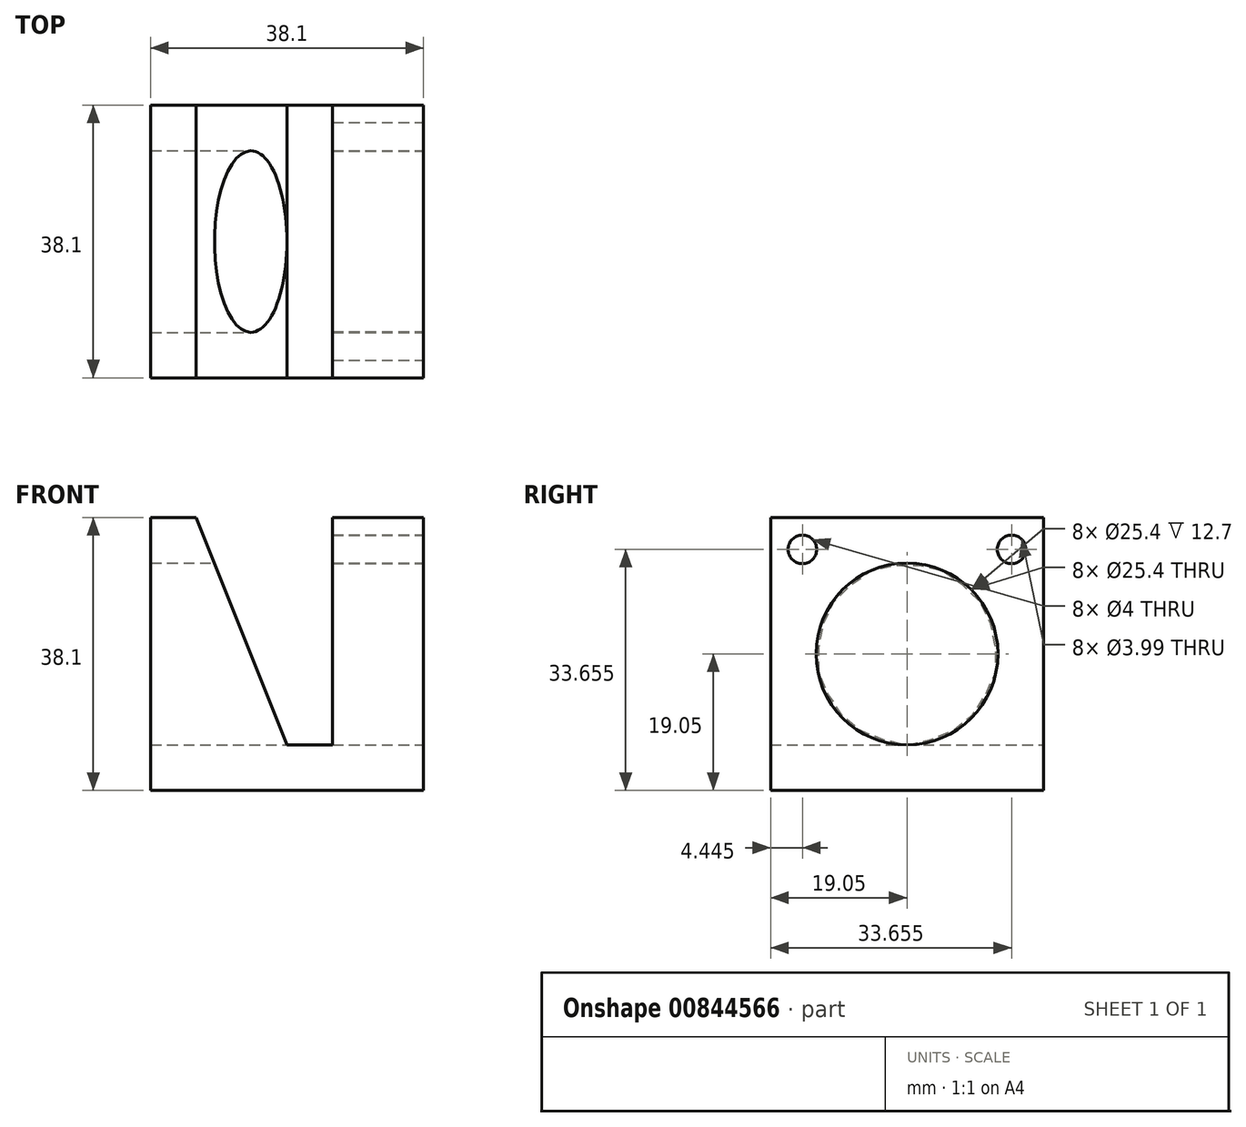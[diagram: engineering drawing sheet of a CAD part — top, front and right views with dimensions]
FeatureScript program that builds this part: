
annotation { "Feature Type Name" : "Feature", "Feature Type Description" : "" }
export const myFeature = defineFeature(function(context is Context, id is Id, definition is map)
    precondition{}
    {
        {
            var Q0;
            Q0=qCreatedBy(makeId("Front.planeOp"),FACE);
            var sketch = newSketch(context, id + "F0", { "sketchPlane" : qUnion([Q0])});
            skLineSegment(sketch, "E0.bottom", {"start": v(19.05, 19.05) * mm, "end": v(-19.05, 19.05) * mm});
            skLineSegment(sketch, "E0.top", {"start": v(19.05, -19.05) * mm, "end": v(-19.05, -19.05) * mm});
            skLineSegment(sketch, "E0.left", {"start": v(19.05, 19.05) * mm, "end": v(19.05, -19.05) * mm});
            skLineSegment(sketch, "E0.right", {"start": v(-19.05, 19.05) * mm, "end": v(-19.05, -19.05) * mm});
            skPoint(sketch, "E0.middle", {"position": v(0, 0) * mm});
            skLineSegment(sketch, "E1", {"start": v(6.35, 19.05) * mm, "end": v(6.35, -12.7) * mm});
            skLineSegment(sketch, "E2", {"start": v(6.35, -12.7) * mm, "end": v(0, -12.7) * mm});
            skLineSegment(sketch, "E3", {"start": v(-12.7, 19.05) * mm, "end": v(0, -12.7) * mm});
            skLineSegment(sketch, "E4", {"start": v(-12.7, 19.05) * mm, "end": v(-19.05, 19.05) * mm});
            skLineSegment(sketch, "E5", {"start": v(-12.7, 19.05) * mm, "end": v(-6.35, 19.05) * mm});
            skSolve(sketch);
        }
        {
            var Q0;
            Q0=makeQuery(id+"F0.imprint","IMPRINT",FACE,{"disambiguationData":[TD([[makeQuery(id+"F0.imprint","IMPRINT",EDGE,{"derivedFrom":sQuery(id+"F0.wireOp",EDGE,"E0.top")}),-1.0]])]});
            extrude(context, id + "F1", {"entities" : qUnion([Q0]), "endBound" : BoundingType.SYMMETRIC, "depth" : 38.1 * mm, "offsetDistance" : 25.4 * mm});
        }
        {
            var Q0;
            Q0=makeQuery(id+"F1.opExtrude","SWEPT_FACE",FACE,{"disambiguationData":[OSD([sQuery(id+"F0.wireOp",EDGE,"E0.left")])]});
            var sketch = newSketch(context, id + "F2", { "sketchPlane" : qUnion([Q0])});
            skCircle(sketch, "E6", {"center": v(0, 0) * mm, "radius": 12.7 * mm});
            skCircle(sketch, "E7", {"center": v(-14.6, 14.6) * mm, "radius": 2 * mm});
            skCircle(sketch, "E8", {"center": v(14.6, 14.6) * mm, "radius": 2 * mm});
            skSolve(sketch);
        }
        {
            var Q0;
            Q0=makeQuery(id+"F2.imprint","IMPRINT",FACE,{"disambiguationData":[TD([[makeQuery(id+"F2.imprint","IMPRINT",EDGE,{"derivedFrom":sQuery(id+"F2.wireOp",EDGE,"E6")}),1.0]])]});
            extrude(context, id + "F3", {"entities" : qUnion([Q0]), "operationType" : NewBodyOperationType.REMOVE, "oppositeDirection" : true, "depth" : 38.1 * mm, "offsetDistance" : 25.4 * mm});
        }
        {
            var Q0;
            Q0=makeQuery(id+"F2.imprint","IMPRINT",FACE,{"disambiguationData":[TD([[makeQuery(id+"F2.imprint","IMPRINT",EDGE,{"derivedFrom":sQuery(id+"F2.wireOp",EDGE,"E8")}),1.0]])]});
            var Q1;
            Q1=makeQuery(id+"F2.imprint","IMPRINT",FACE,{"disambiguationData":[TD([[makeQuery(id+"F2.imprint","IMPRINT",EDGE,{"derivedFrom":sQuery(id+"F2.wireOp",EDGE,"E7")}),1.0]])]});
            var Q2;
            Q2=makeQuery(id+"F2.imprint","IMPRINT",FACE,{"disambiguationData":[TD([[makeQuery(id+"F2.imprint","IMPRINT",EDGE,{"derivedFrom":sQuery(id+"F2.wireOp",EDGE,"rxBmIwr1-k0hV-PaYD-DXjJ-kE9HBhcPyFlo")}),1.0]])]});
            extrude(context, id + "F4", {"entities" : qUnion([Q0, Q1, Q2]), "operationType" : NewBodyOperationType.REMOVE, "oppositeDirection" : true, "depth" : 12.7 * mm, "offsetDistance" : 25.4 * mm});
        }
    });
